# Revit family: Edelstahlrohrschelle V4A, M10, Ø 47-116, Gummi
name_source: partatom
category: HLS-Bauteile
revit_build: Autodesk Revit 2017 (Build: 20190507_1515(x64)
units: mm (PartAtom-declared; Revit-internal decimal feet)

## family parameters
Arbeitsebenenbasiert = Ja
Beim Laden mit Abzugskörper schneiden = Nein
Bemaßung runder Anschluss = Durchmesser verwenden
Gemeinsam genutzt = Ja
Immer vertikal = Nein
Raumberechnungspunkt = Nein
Teiletyp = Normal

## types (9) — shared parameters
A = 16 mm  [stored 0.0524934 ft]
Anschluss = M10
Anschlußhöhe = 16 mm
Bauart = zweiteilig
Baustoffklasse = B2
DF1 = 14 mm  [stored 0.0459318 ft]
DF2 = 14 mm  [stored 0.0459318 ft]
DS = 6 mm  [stored 0.019685 ft]
DVS = 7 mm  [stored 0.0229659 ft]
Dämmstärke = 6 mm  [stored 0.019685 ft]
Fabrikat = MEFA
Farbe Schalldämmeinlage = schwarz
Firma = MEFA Befestigungs- und Montagesysteme GmbH
HGA = 8 mm  [stored 0.0262467 ft]
Kurztext1 = Rohrschelle Edelstahl V4A 20x2,0
MB = 20 mm  [stored 0.0656168 ft]
MD = 2 mm  [stored 0.00656168 ft]
Material = Edelstahl
Material Schalldämmeinlage = TPE
Materialmaße = 20x2,0 mm
Mengeneinheit = St
Schalldämmeinlage = Gummi
Verschluss = Schraubenverschluss
Verschluss-Schraube = M6
Vorgabe-Ansicht = 1219 mm
max. Temperaturbeständigkeit = 100 °C
max. zul. Last horizontal = 0.00 kN
max. zul. Last vertikal = 0.00 kN
vpe = 50 St
zero-valued in all types: Nennweite DN Rohr, Rohraußendurchmesser, Stärke Material

## per-type parameters (varying)
| type | AB | Achsabstand | Artikelnummer | B | D | D0 | Dmax | Dmin | EAN | Gewicht | Gewicht pro Bauteil | H | Kurztext2 | R | RM | Rohraußendurchmesser Zoll | S | max. Rohraußendurchmesser | min. Rohraußendurchmesser |
| Edelstahlrohrschelle V4A, M10, Ø 47- 52, Gummi | 5 mm  [stored 0.0164042 ft] | 82 mm | 0498210 | 96 mm | 52 mm | 64 mm  [stored 0.209974 ft] | 52 mm | 47 mm  [stored 0.154199 ft] | 4250928413833 | 0.13 kg | 0.13 kg | 76 mm  [stored 0.249344 ft] | 47 - 52 mm M10 TPE | 32 mm  [stored 0.104987 ft] | 34 mm | 1 1/2 Zoll | 82 mm  [stored 0.269029 ft] | 52 mm | 47 mm  [stored 0.154199 ft] |
| Edelstahlrohrschelle V4A, M10, Ø 53- 57, Gummi | 4 mm  [stored 0.0131234 ft] | 88 mm | 0498211 | 101 mm | 57 mm  [stored 0.187008 ft] | 69 mm  [stored 0.226378 ft] | 57 mm  [stored 0.187008 ft] | 53 mm  [stored 0.173885 ft] | 4250928413840 | 0.13 kg | 0.13 kg | 81 mm  [stored 0.265748 ft] | 53 - 57 mm M10 TPE | 35 mm | 37 mm | Zoll | 87 mm  [stored 0.285433 ft] | 57 mm  [stored 0.187008 ft] | 53 mm  [stored 0.173885 ft] |
| Edelstahlrohrschelle V4A, M10, Ø 58- 64, Gummi | 6 mm  [stored 0.019685 ft] | 94 mm | 0498212 | 108 mm | 64 mm  [stored 0.209974 ft] | 76 mm  [stored 0.249344 ft] | 64 mm  [stored 0.209974 ft] | 58 mm  [stored 0.190289 ft] | 4250928413857 | 0.14 kg | 0.14 kg | 88 mm | 58 - 64 mm M10 TPE | 38 mm  [stored 0.124672 ft] | 40 mm  [stored 0.131234 ft] | 2 Zoll | 94 mm | 64 mm  [stored 0.209974 ft] | 58 mm  [stored 0.190289 ft] |
| Edelstahlrohrschelle V4A, M10, Ø 65- 70, Gummi | 5 mm  [stored 0.0164042 ft] | 101 mm | 0498213 | 114 mm | 70 mm  [stored 0.229659 ft] | 82 mm  [stored 0.269029 ft] | 70 mm  [stored 0.229659 ft] | 65 mm  [stored 0.213255 ft] | 4250928413864 | 0.15 kg | 0.15 kg | 94 mm | 65 - 70 mm M10 TPE | 41 mm  [stored 0.134514 ft] | 43 mm  [stored 0.141076 ft] | Zoll | 100 mm | 70 mm  [stored 0.229659 ft] | 65 mm  [stored 0.213255 ft] |
| Edelstahlrohrschelle V4A, M10, Ø 72- 80, Gummi | 8 mm  [stored 0.0262467 ft] | 110 mm | 0498214 | 124 mm | 80 mm  [stored 0.262467 ft] | 92 mm | 80 mm  [stored 0.262467 ft] | 72 mm  [stored 0.23622 ft] | 4250928413871 | 0.16 kg | 0.16 kg | 104 mm | 72 - 80 mm M10 TPE | 46 mm  [stored 0.150919 ft] | 48 mm  [stored 0.15748 ft] | 2 1/2 Zoll | 110 mm | 80 mm  [stored 0.262467 ft] | 72 mm  [stored 0.23622 ft] |
| Edelstahlrohrschelle V4A, M10, Ø 82- 90, Gummi | 8 mm  [stored 0.0262467 ft] | 120 mm | 0498215 | 134 mm | 90 mm | 102 mm | 90 mm | 82 mm  [stored 0.269029 ft] | 4250928413888 | 0.18 kg | 0.18 kg | 114 mm | 82 - 90 mm M10 TPE | 51 mm  [stored 0.167323 ft] | 53 mm  [stored 0.173885 ft] | 3 Zoll | 120 mm | 90 mm | 82 mm  [stored 0.269029 ft] |
| Edelstahlrohrschelle V4A, M10, Ø 93-100, Gummi | 7 mm  [stored 0.0229659 ft] | 130 mm | 0498216 | 144 mm | 100 mm | 112 mm | 100 mm | 93 mm | 4250928413895 | 0.19 kg | 0.19 kg | 124 mm | 93 - 100 mm M10 TPE | 56 mm  [stored 0.183727 ft] | 58 mm  [stored 0.190289 ft] | Zoll | 130 mm | 100 mm | 93 mm |
| Edelstahlrohrschelle V4A, M10, Ø102-107, Gummi | 5 mm  [stored 0.0164042 ft] | 138 mm | 0498217 | 151 mm | 107 mm | 119 mm | 107 mm | 102 mm | 4250928413901 | 0.20 kg | 0.20 kg | 131 mm | 102 - 107 mm M10 TPE | 60 mm  [stored 0.19685 ft] | 62 mm  [stored 0.203412 ft] | Zoll | 137 mm | 107 mm | 102 mm |
| Edelstahlrohrschelle V4A, M10, Ø108-116, Gummi | 8 mm  [stored 0.0262467 ft] | 147 mm | 0498218 | 160 mm | 116 mm | 128 mm | 116 mm | 108 mm | 4250928413918 | 0.21 kg | 0.21 kg | 140 mm | 108 - 116 mm M10 TPE | 64 mm  [stored 0.209974 ft] | 66 mm  [stored 0.216535 ft] | 4 Zoll | 146 mm | 116 mm | 108 mm |

note: [stored X ft] marks values corroborated as IEEE doubles in the binary element streams (Revit-internal decimal feet)

## geometry (parser evidence)
native form markers: Sweep x6
no freeform markers — native parametric forms only
